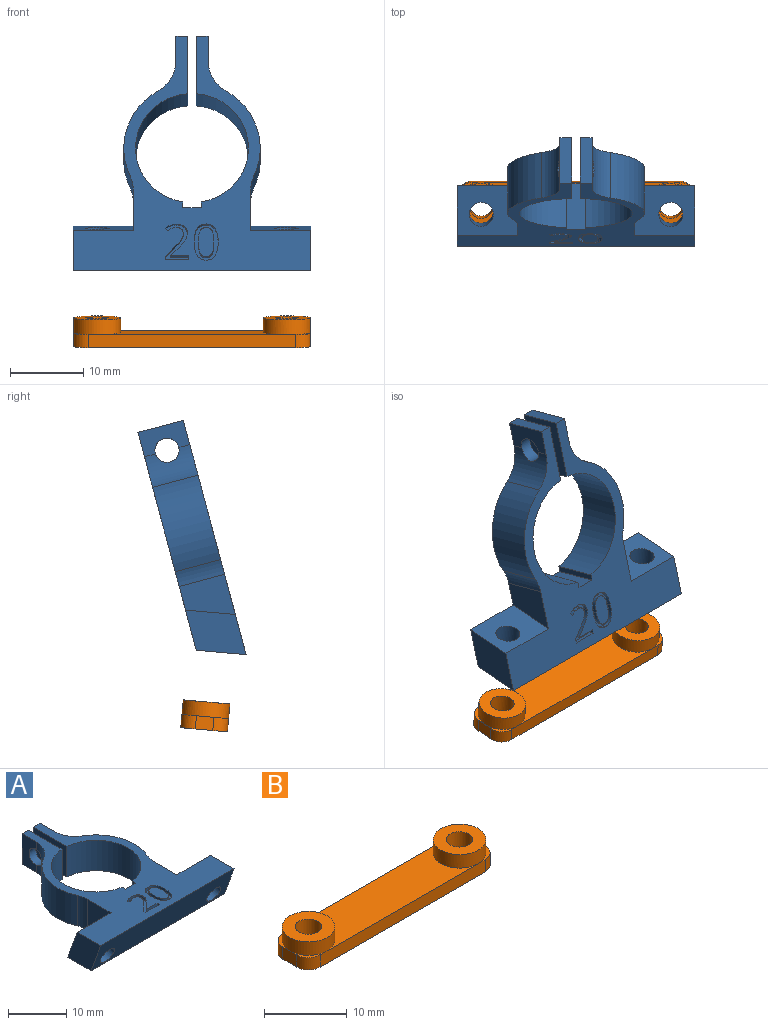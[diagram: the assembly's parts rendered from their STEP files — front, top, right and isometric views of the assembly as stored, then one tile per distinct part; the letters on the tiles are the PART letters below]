
ASSEMBLY  parts=2 mates=1
PART A: 69 faces, bbox 32.4x33.1x6.4 mm
  f0: plane 33.1x32.4mm, normal (0,0,1), area 329.4mm2, adj f1,f3,f4,f5,f6,f7,f9,f10
  f1: plane 8x6.4mm, normal (1,0,0), area 36.3mm2, adj f0,f8,f22,f25
  f2: cylinder r=1.65mm len=6.14mm, axis (0,-0.94,-0.34), area 55.2mm2, adj f22,f25
  f3: plane 8x6.4mm, normal (-1,0,0), area 36.3mm2, adj f0,f8,f22,f24
  f4: cylinder r=9.3mm len=11.91mm, axis (0,0,-1), area 87.7mm2, adj f0,f8,f65,f67
  f5: cylinder r=9.3mm len=11.91mm, axis (0,0,-1), area 87.7mm2, adj f0,f8,f66,f68
  f6: cylinder r=7.7mm len=15.27mm, axis (0,0,-1), area 142.9mm2, adj f0,f8,f10,f13
  f7: cylinder r=7.7mm len=15.27mm, axis (0,0,-1), area 142.9mm2, adj f0,f8,f9,f12
  f8: plane 32.4x30.77mm, normal (0,0,-1), area 311.5mm2, adj f1,f3,f4,f5,f6,f7,f9,f10
  f9: plane 6.4x0.8mm, normal (-1,0,0), area 5.1mm2, adj f0,f7,f8,f11
  f10: plane 6.4x0.8mm, normal (1,0,0), area 5.1mm2, adj f0,f6,f8,f11
  f11: plane 6.4x2.5mm, normal (0,1,0), area 16mm2, adj f0,f8,f9,f10
  f12: plane 8.12x6.4mm, normal (-1,0,0), area 43.4mm2, adj f0,f7,f8,f17,f18
  f13: plane 8.12x6.4mm, normal (1,0,0), area 43.4mm2, adj f0,f6,f8,f15,f19
  f14: plane 6.4x3.45mm, normal (-1,0,0), area 17.6mm2, adj f0,f8,f15,f19,f66
  f15: plane 6.4x1.6mm, normal (0,1,0), area 10.2mm2, adj f0,f8,f13,f14
  f16: plane 6.4x3.45mm, normal (1,0,0), area 17.6mm2, adj f0,f8,f17,f18,f65
  f17: plane 6.4x1.6mm, normal (0,1,0), area 10.2mm2, adj f0,f8,f12,f16
  f18: cylinder r=1.65mm len=3.3mm, axis (-1,0,0), area 17.2mm2, adj f12,f16,f65
  f19: cylinder r=1.65mm len=3.3mm, axis (-1,0,0), area 17.2mm2, adj f13,f14,f66
  f20: plane 6.4x5.67mm, normal (1,0,0), area 28.8mm2, adj f0,f8,f25,f67
  f21: plane 6.4x5.67mm, normal (-1,0,0), area 28.8mm2, adj f0,f8,f24,f68
  f22: plane 32.4x6.4mm, normal (0,-0.94,-0.34), area 203.6mm2, adj f0,f1,f2,f3,f8,f23
  f23: cylinder r=1.65mm len=6.14mm, axis (0,-0.94,-0.34), area 55.2mm2, adj f22,f24
  f24: plane 8.2x6.4mm, normal (0,0.94,0.34), area 47.3mm2, adj f0,f3,f8,f21,f23
  f25: plane 8.2x6.4mm, normal (0,0.94,0.34), area 47.3mm2, adj f0,f1,f2,f8,f20
  f26: extruded ~1.58x0.6mm, area 1mm2, adj f27,f41,f42,f64
  f27: extruded ~1.57x0.6mm, area 1mm2, adj f26,f28,f42,f64
  f28: extruded ~0.81x0.6mm, area 0.6mm2, adj f27,f29,f42,f64
  f29: extruded ~0.82x0.6mm, area 0.6mm2, adj f28,f30,f42,f64
  f30: extruded ~1.56x0.6mm, area 1mm2, adj f29,f31,f42,f64
  f31: extruded ~1.57x0.6mm, area 1mm2, adj f30,f32,f42,f64
  f32: extruded ~0.82x0.6mm, area 0.6mm2, adj f31,f41,f42,f64
  f33: extruded ~1.92x0.6mm, area 1.2mm2, adj f0,f34,f40,f42
  f34: extruded ~1.9x0.6mm, area 1.2mm2, adj f0,f33,f35,f42
  f35: extruded ~1.23x0.66mm, area 0.9mm2, adj f0,f34,f36,f42
  f36: extruded ~1.23x0.63mm, area 0.9mm2, adj f0,f35,f37,f42
  f37: extruded ~1.92x0.6mm, area 1.2mm2, adj f0,f36,f38,f42
  f38: extruded ~1.91x0.6mm, area 1.2mm2, adj f0,f37,f39,f42
  f39: extruded ~1.22x0.65mm, area 0.9mm2, adj f0,f38,f40,f42
  f40: extruded ~1.24x0.63mm, area 0.9mm2, adj f0,f33,f39,f42
  f41: extruded ~0.81x0.6mm, area 0.6mm2, adj f26,f32,f42,f64
  f42: plane 5.1x3.28mm, normal (0,0,1), area 6.5mm2, adj f26,f27,f28,f29,f30,f31,f32,f33
  f43: plane 3.26x0.6mm, normal (0,1,0), area 2mm2, adj f0,f44,f62,f63
  f44: plane 0.6x0.52mm, normal (-1,0,0), area 0.3mm2, adj f0,f43,f45,f63
  f45: plane 2.55x0.6mm, normal (0,-1,0), area 1.5mm2, adj f0,f44,f46,f63
  f46: plane 0.6x0.03mm, normal (-1,0,0), area 0mm2, adj f0,f45,f47,f63
  f47: plane 1.09x1.06mm, normal (-0.7,0.71,0), area 0.9mm2, adj f0,f46,f48,f63
  f48: extruded ~1.17x0.99mm, area 0.9mm2, adj f0,f47,f49,f63
  f49: extruded ~0.93x0.6mm, area 0.6mm2, adj f0,f48,f50,f63
  f50: extruded ~0.96x0.6mm, area 0.6mm2, adj f0,f49,f51,f63
  f51: extruded ~1.1x0.6mm, area 0.7mm2, adj f0,f50,f52,f63
  f52: extruded ~1.49x0.6mm, area 1mm2, adj f0,f51,f53,f63
  f53: plane 0.6x0.38mm, normal (0.79,0.61,0), area 0.3mm2, adj f0,f52,f54,f63
  f54: extruded ~0.62x0.6mm, area 0.4mm2, adj f0,f53,f55,f63
  f55: extruded ~0.6x0.59mm, area 0.4mm2, adj f0,f54,f56,f63
  f56: extruded ~0.67x0.6mm, area 0.4mm2, adj f0,f55,f57,f63
  f57: extruded ~0.63x0.6mm, area 0.4mm2, adj f0,f56,f58,f63
  f58: extruded ~0.6x0.53mm, area 0.3mm2, adj f0,f57,f59,f63
  f59: extruded ~0.6x0.5mm, area 0.3mm2, adj f0,f58,f60,f63
  f60: extruded ~0.86x0.79mm, area 0.7mm2, adj f0,f59,f61,f63
  f61: plane 1.31x1.31mm, normal (0.71,-0.71,0), area 1.1mm2, adj f0,f60,f62,f63
  f62: plane 0.6x0.49mm, normal (1,0,0), area 0.3mm2, adj f0,f43,f61,f63
  f63: plane 5.03x3.26mm, normal (0,0,1), area 5.4mm2, adj f43,f44,f45,f46,f47,f48,f49,f50
  f64: plane 4.13x2.13mm, normal (0,0,1), area 7.4mm2, adj f26,f27,f28,f29,f30,f31,f32,f41
  f65: cylinder r=5mm len=6.4mm, axis (0,0,-1), area 29.3mm2, adj f0,f4,f8,f16,f18
  f66: cylinder r=5mm len=6.4mm, axis (0,0,-1), area 29.3mm2, adj f0,f5,f8,f14,f19
  f67: cylinder r=5mm len=6.4mm, axis (0,0,-1), area 13.8mm2, adj f0,f4,f8,f20
  f68: cylinder r=5mm len=6.4mm, axis (0,0,-1), area 13.8mm2, adj f0,f5,f8,f21
PART B: 20 faces, bbox 32.3x6.4x3.8 mm
  f0: plane 3.19x3.19mm, normal (0,0,1), area 1.3mm2, adj f5,f6,f13,f18
  f1: plane 3.19x3.19mm, normal (0,0,1), area 1.3mm2, adj f4,f5,f12,f18
  f2: plane 25.87x6.39mm, normal (0,0,1), area 133.2mm2, adj f4,f6,f16,f18
  f3: plane 3.19x3.19mm, normal (0,0,1), area 1.3mm2, adj f4,f8,f15,f16
  f4: plane 28.26x1.8mm, normal (0,-1,0), area 50.9mm2, adj f1,f2,f3,f10,f12,f15
  f5: plane 2.39x1.8mm, normal (-1,0,0), area 4.3mm2, adj f0,f1,f10,f12,f13
  f6: plane 28.26x1.8mm, normal (0,1,0), area 50.9mm2, adj f0,f2,f10,f11,f13,f14
  f7: cylinder r=1.6mm len=3.8mm, axis (0,0,1), area 38.2mm2, adj f10,f17
  f8: plane 2.39x1.8mm, normal (1,0,0), area 4.3mm2, adj f3,f10,f11,f14,f15
  f9: cylinder r=1.6mm len=3.8mm, axis (0,0,1), area 38.2mm2, adj f10,f19
  f10: plane 32.26x6.39mm, normal (0,0,-1), area 186.5mm2, adj f4,f5,f6,f7,f8,f9,f12,f13
  f11: plane 3.19x3.19mm, normal (0,0,1), area 1.3mm2, adj f6,f8,f14,f16
  f12: cylinder r=2mm len=2mm, axis (0,0,-1), area 5.7mm2, adj f1,f4,f5,f10
  f13: cylinder r=2mm len=2mm, axis (0,0,1), area 5.7mm2, adj f0,f5,f6,f10
  f14: cylinder r=2mm len=2mm, axis (0,0,-1), area 5.7mm2, adj f6,f8,f10,f11
  f15: cylinder r=2mm len=2mm, axis (0,0,1), area 5.7mm2, adj f3,f4,f8,f10
  f16: cylinder r=3.19mm len=6.39mm, axis (0,0,-1), area 40.1mm2, adj f2,f3,f11,f17
  f17: plane 6.39x6.39mm, normal (0,0,1), area 24mm2, adj f7,f16
  f18: cylinder r=3.19mm len=6.39mm, axis (0,0,-1), area 40.1mm2, adj f0,f1,f2,f19
  f19: plane 6.39x6.39mm, normal (0,0,1), area 24mm2, adj f9,f18
PLACE A rot(axis=(1,0,0),75deg) t=(3.08,15.14,24.05)mm
PLACE B rot(axis=(1,0,0),5deg) t=(3.08,-49.98,-3.7)mm
MATE cylindrical A.f2 <-> B.f7  axis (0,0.09,-1) through (16.02,9.27,9.42)mm
